# Revit family: York CB-ABW-YK - Sidewall Active Chilled Beam, Face Base, Revit 2015 R1.0
name_source: partatom
category: Mechanical Equipment
revit_build: Autodesk Revit 2015 (Build: 20160512_1515(x64)
units: mm (PartAtom-declared; Revit-internal decimal feet)

## types (1)
- CB-ABW-YK
    (0) Front and Back Supply = Yes
    (1) Front Supply = No
    (2) Back Supply = No
    0 - No Insulation = Yes
    10 ft = Yes
    2 ft = No
    26 - White = Yes
    2P1C - 2 Pipe Coil = Yes
    3 ft = No
    4 ft = No
    4" Dia. = No
    4P1C - 4 Pipe Coil = No
    5 ft = No
    5" Dia. = No
    6 ft = No
    6" Dia. = Yes
    7 ft = No
    8 ft = No
    8" Oval Inlet = No
    84 - Black Paint = No
    9 ft = No
    A = 120"
    A - Other Nominal Length = 24"
    Angle L = 59"
    Angle of Hot Water = 180.00°
    Angle of cold water = 0.00°
    B = 5 7/8"
    B - Other Nominal Inlet = 3 7/8"
    B1 = Yes
    B2 = No
    B3 = No
    B4 = No
    Blade Length = 115 109/256"
    C = 122 1/8"
    C - Other Nominal Length = 122 1/8"
    Circular Inlet Visible = Yes
    Circular Perforation = Yes
    Clearance = Clearance
    Clearance border = 4"
    Cold Pipe Dia = 1/2"
    Cold Water Pipe R = 1/4"
    Default Elevation = 48"
    Description = Sidewall / Bulkhead Mounted Active Chilled Beam
    H12 - SS Flex Hose - 12 inch = No
    H18 - SS Flex Hose - 18 inch = No
    H24 - SS Flex Hose - 24 inch = No
    Hot Pipe Dia = 1/2"
    Hot Water pipe R = 1/4"
    L - Left Hand = Yes
    L - ½ in Ecosheild (Foil Face) = No
    Linear Bar Grille = No
    MPT - Male Pipe Thread = No
    Manufacturer = York
    Material = Casing:  G90 20GA Galvanealed sheet metal
    Model = CB-ABW-YK, 2 - Pipe Coil, Left Hand
    Neck Size = 0"
    Outer Flange W = 10 1/2"
    Oval Inlet Visible = No
    Perforated Circle R = 1/4"
    Pipe Connector Cold Return = CWR
    Pipe Connector Hot Return = HWR
    Pipe Connector Hot Supply = HWF
    Pipe Connector cold Supply = CWF
    R - Right Hand = No
    SWT - Sweat = Yes
    Select a Nominal Beam Length = 9
    Select a Pipe Connection Type = 1
    Select a Return Grille Type = 2
    Select a Water-Coil Type = 1
    Select an Air Nozzle Configuration = 1
    Select the Nominal Air Inlet Size = 3
    Select the Plenum Liner (External) = 1
    Select the Water-Coil Connection Side = 1
    URL = http://www.york.com
    Water Connection Location Selection = 0
    X Blade distance = 1/2"

## geometry (parser evidence)
native form markers: Blend x2, Sweep x4
no freeform markers — native parametric forms only
